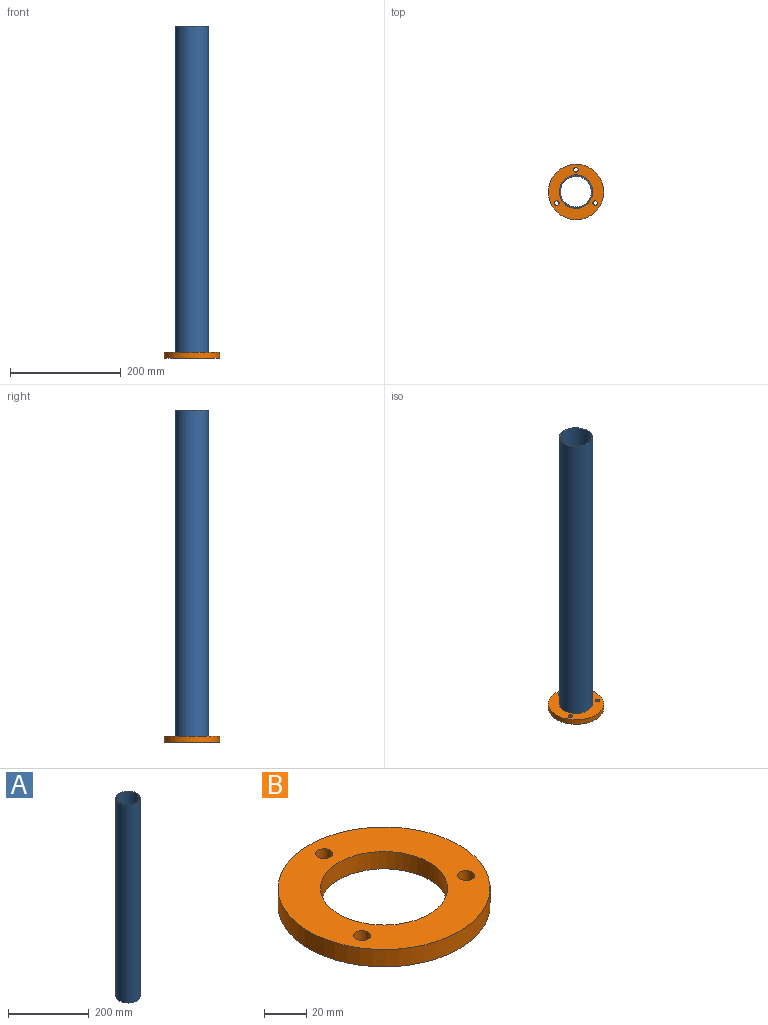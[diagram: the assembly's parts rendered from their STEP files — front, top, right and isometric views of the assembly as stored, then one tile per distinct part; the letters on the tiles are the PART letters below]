
ASSEMBLY  parts=2 mates=1
PART A: 4 faces, bbox 60x60x600 mm
  f0: cylinder r=28mm len=600mm, axis (0,0,-1), area 105557.5mm2, adj f2,f3
  f1: cylinder r=30mm len=600mm, axis (0,0,-1), area 113097.3mm2, adj f2,f3
  f2: plane 60x60mm, normal (0,0,1), area 364.4mm2, adj f0,f1
  f3: plane 60x60mm, normal (0,0,-1), area 364.4mm2, adj f0,f1
PART B: 7 faces, bbox 100x100x10 mm
  f0: cylinder r=30mm len=60mm, axis (0,0,-1), area 1885mm2, adj f2,f3
  f1: cylinder r=50mm len=100mm, axis (0,0,-1), area 3141.6mm2, adj f2,f3
  f2: plane 100x100mm, normal (0,0,1), area 4875.8mm2, adj f0,f1,f4,f5,f6
  f3: plane 100x100mm, normal (0,0,-1), area 4875.8mm2, adj f0,f1,f4,f5,f6
  f4: cylinder r=4mm len=10mm, axis (0,0,1), area 251.3mm2, adj f2,f3
  f5: cylinder r=4mm len=10mm, axis (0,0,1), area 251.3mm2, adj f2,f3
  f6: cylinder r=4mm len=10mm, axis (0,0,1), area 251.3mm2, adj f2,f3
PLACE A t=(-239.35,21.46,-60.53)mm
PLACE B t=(-239.35,21.46,-60.53)mm fixed
MATE fastened B.f1 <-> A.f0  axis (0,0,-1) through (-239.35,21.46,-60.53)mm
